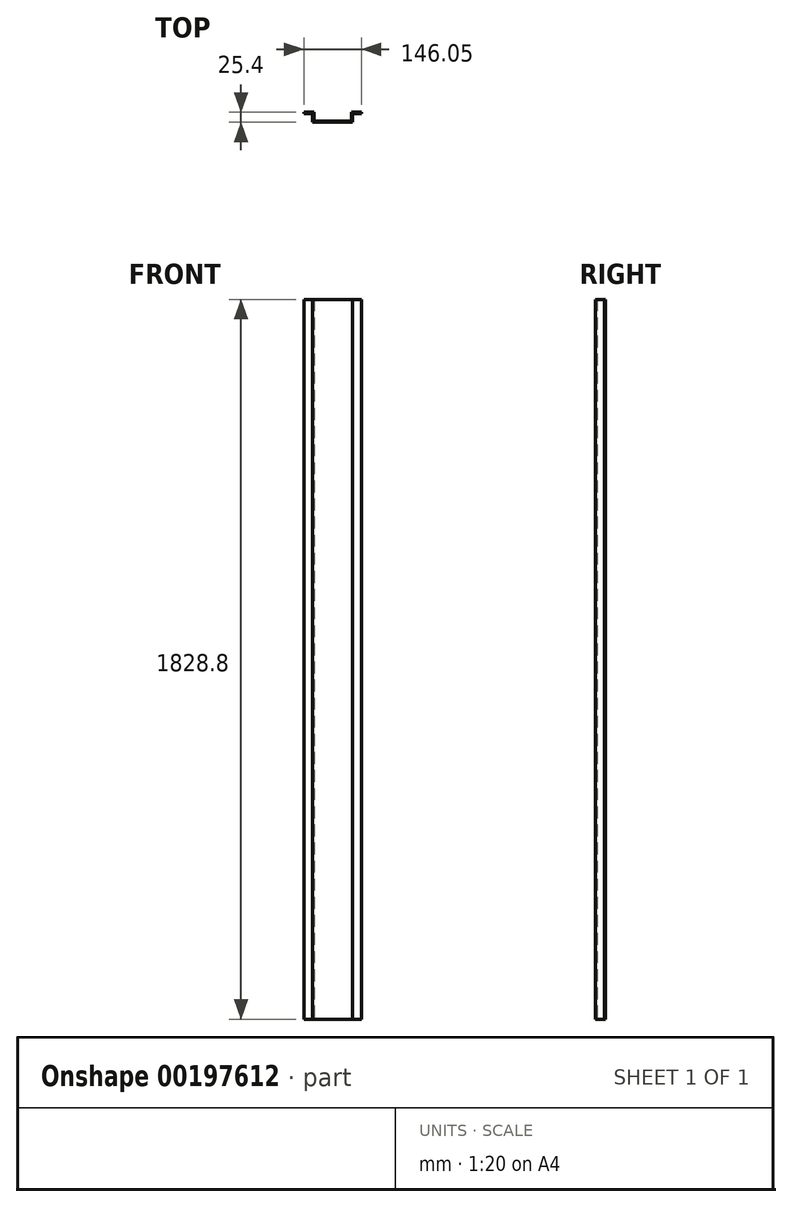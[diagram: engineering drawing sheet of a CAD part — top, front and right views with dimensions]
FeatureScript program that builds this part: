
annotation { "Feature Type Name" : "Feature", "Feature Type Description" : "" }
export const myFeature = defineFeature(function(context is Context, id is Id, definition is map)
    precondition{}
    {
        {
            var Q0;
            Q0=qCreatedBy(makeId("Top.planeOp"),FACE);
            var sketch = newSketch(context, id + "F0", { "sketchPlane" : qUnion([Q0])});
            skLineSegment(sketch, "E0", {"start": v(-56.3, 15.71) * mm, "end": v(-34.08, 15.71) * mm});
            skLineSegment(sketch, "E1", {"start": v(-34.08, 15.71) * mm, "end": v(-34.08, -6.51) * mm});
            skLineSegment(sketch, "E2", {"start": v(-34.08, -6.51) * mm, "end": v(67.52, -6.51) * mm});
            skLineSegment(sketch, "E3", {"start": v(67.52, -6.51) * mm, "end": v(67.52, 15.71) * mm});
            skLineSegment(sketch, "E4", {"start": v(67.52, 15.71) * mm, "end": v(89.75, 15.71) * mm});
            skLineSegment(sketch, "E5.0", {"start": v(64.35, 18.89) * mm, "end": v(89.75, 18.89) * mm});
            skLineSegment(sketch, "E5.1", {"start": v(-56.3, 18.89) * mm, "end": v(-30.9, 18.89) * mm});
            skLineSegment(sketch, "E5.2", {"start": v(-30.9, 18.89) * mm, "end": v(-30.9, -3.34) * mm});
            skLineSegment(sketch, "E5.3", {"start": v(-30.9, -3.34) * mm, "end": v(64.35, -3.34) * mm});
            skLineSegment(sketch, "E5.4", {"start": v(64.35, -3.34) * mm, "end": v(64.35, 18.89) * mm});
            skLineSegment(sketch, "E6", {"start": v(-56.3, 18.89) * mm, "end": v(-56.3, 15.71) * mm});
            skLineSegment(sketch, "E7", {"start": v(89.75, 18.89) * mm, "end": v(89.75, 15.71) * mm});
            skSolve(sketch);
        }
        {
            var Q0;
            Q0=makeQuery(id+"F0.imprint","IMPRINT",FACE,{"disambiguationData":[TD([[makeQuery(id+"F0.imprint","IMPRINT",EDGE,{"derivedFrom":sQuery(id+"F0.wireOp",EDGE,"E0")}),1.0]])]});
            extrude(context, id + "F1", {"entities" : qUnion([Q0]), "depth" : 1828.8 * mm});
        }
    });
